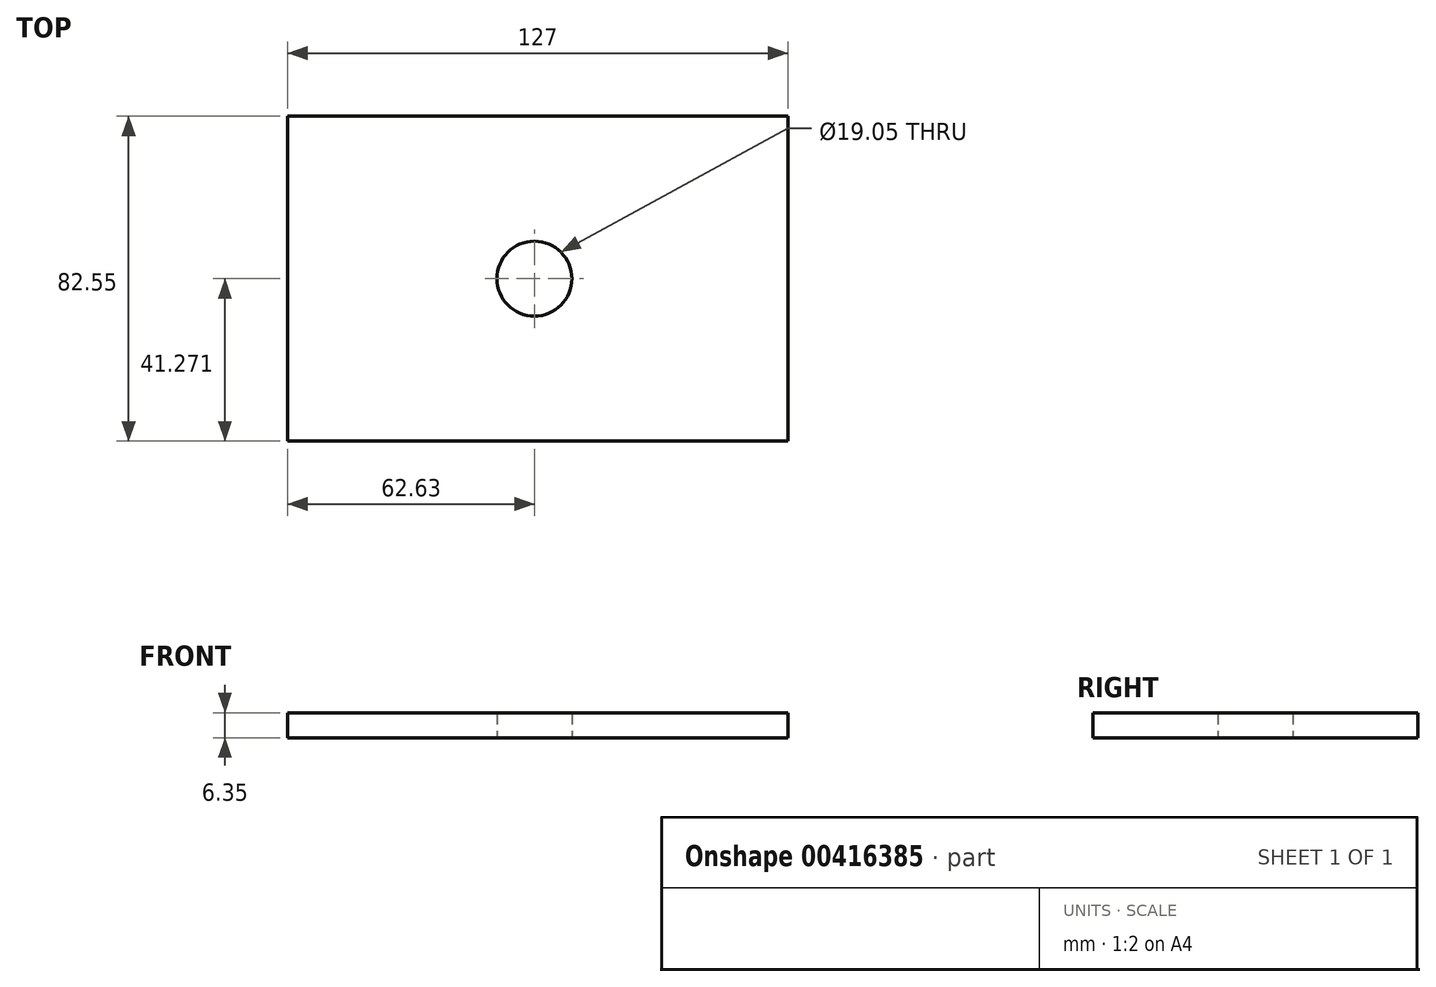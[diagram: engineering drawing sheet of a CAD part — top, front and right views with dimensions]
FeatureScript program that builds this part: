
annotation { "Feature Type Name" : "Feature", "Feature Type Description" : "" }
export const myFeature = defineFeature(function(context is Context, id is Id, definition is map)
    precondition{}
    {
        {
            var Q0;
            Q0=qCreatedBy(makeId("Top.planeOp"),FACE);
            var sketch = newSketch(context, id + "F0", { "sketchPlane" : qUnion([Q0])});
            skLineSegment(sketch, "E0.bottom", {"start": v(-62.63, 14.39) * mm, "end": v(64.37, 14.39) * mm});
            skLineSegment(sketch, "E0.top", {"start": v(-62.63, -68.16) * mm, "end": v(64.37, -68.16) * mm});
            skLineSegment(sketch, "E0.left", {"start": v(-62.63, 14.39) * mm, "end": v(-62.63, -68.16) * mm});
            skLineSegment(sketch, "E0.right", {"start": v(64.37, 14.39) * mm, "end": v(64.37, -68.16) * mm});
            skPoint(sketch, "E1.endSnap0", {"position": v(64.37, -26.89) * mm});
            skCircle(sketch, "E2", {"center": v(0, -26.89) * mm, "radius": 9.53 * mm});
            skSolve(sketch);
        }
        {
            var Q0;
            Q0=makeQuery(id+"F0.imprint","IMPRINT",FACE,{"disambiguationData":[TD([[makeQuery(id+"F0.imprint","IMPRINT",EDGE,{"derivedFrom":sQuery(id+"F0.wireOp",EDGE,"E0.bottom")}),-1.0]])]});
            extrude(context, id + "F1", {"entities" : qUnion([Q0]), "depth" : 6.35 * mm});
        }
    });
